# Revit family: Shower-Modular_Column-KOHLER-Spaviva-K-EX31845T_1
name_source: partatom
category: Plumbing Fixtures
units: mm (PartAtom-declared; Revit-internal decimal feet)

## family parameters
Cut with Voids When Loaded = No
Host = Face
Maintain Annotation Orientation = No
OmniClass Number = 23.31.17.00
OmniClass Title = Showers
Part Type = Normal
Room Calculation Point = No
Round Connector Dimension = Use Diameter
Shared = No

## types (2) — shared parameters
ADA Compliant = No
Assembly Code = D2010700
CW Connection = Yes
Cold Water Inlet = Cold Water Inlet
Date Modified = 04/15/2024
Default Elevation = 42"
Description = Modular Column - Basic Version
Drain Included = No
Flow Rate = 3 GPM
HW Connection = Yes
Height = 45 11/16"
Hot Water Inlet = Hot Water Inlet
Length = 18 9/16"
Manufacturer = Kohler Co.
Master Format 2014 = 22 42 23
Master Format 2014 Name = Residential Showers
Material = Premium Metal Construction
Pressure = 0.00 psi
Product Name = Spaviva
URL = http://www.kohler.com.cn
Vent Connection = No
Waste Connection = No
Waste Water Outlet = Waste Water Outlet
WaterSense Certified = No
Width = 23 13/16"

## per-type parameters (varying)
| type | Finish | Model | Nozzle Finish | Secondary Finish | Type |
| CP-Polished Chrome | Kohler-Metal-CP-Polished_Chrome | K-EX31845T-9-CP | Plastic-Pantone-RAL-9010 | Plastic-Pantone-PQ-11-4800-TCX | 2 |
| BL-Matte Black | Kohler-Metal-BL-Matte_Black | K-EX31845T-9-BL | Plastic-Pantone-PQ-194205-TCX | Plastic-Pantone-PQ-194205-TCX | 1 |

## geometry (parser evidence)
native form markers: Sweep x9
no freeform markers — native parametric forms only
